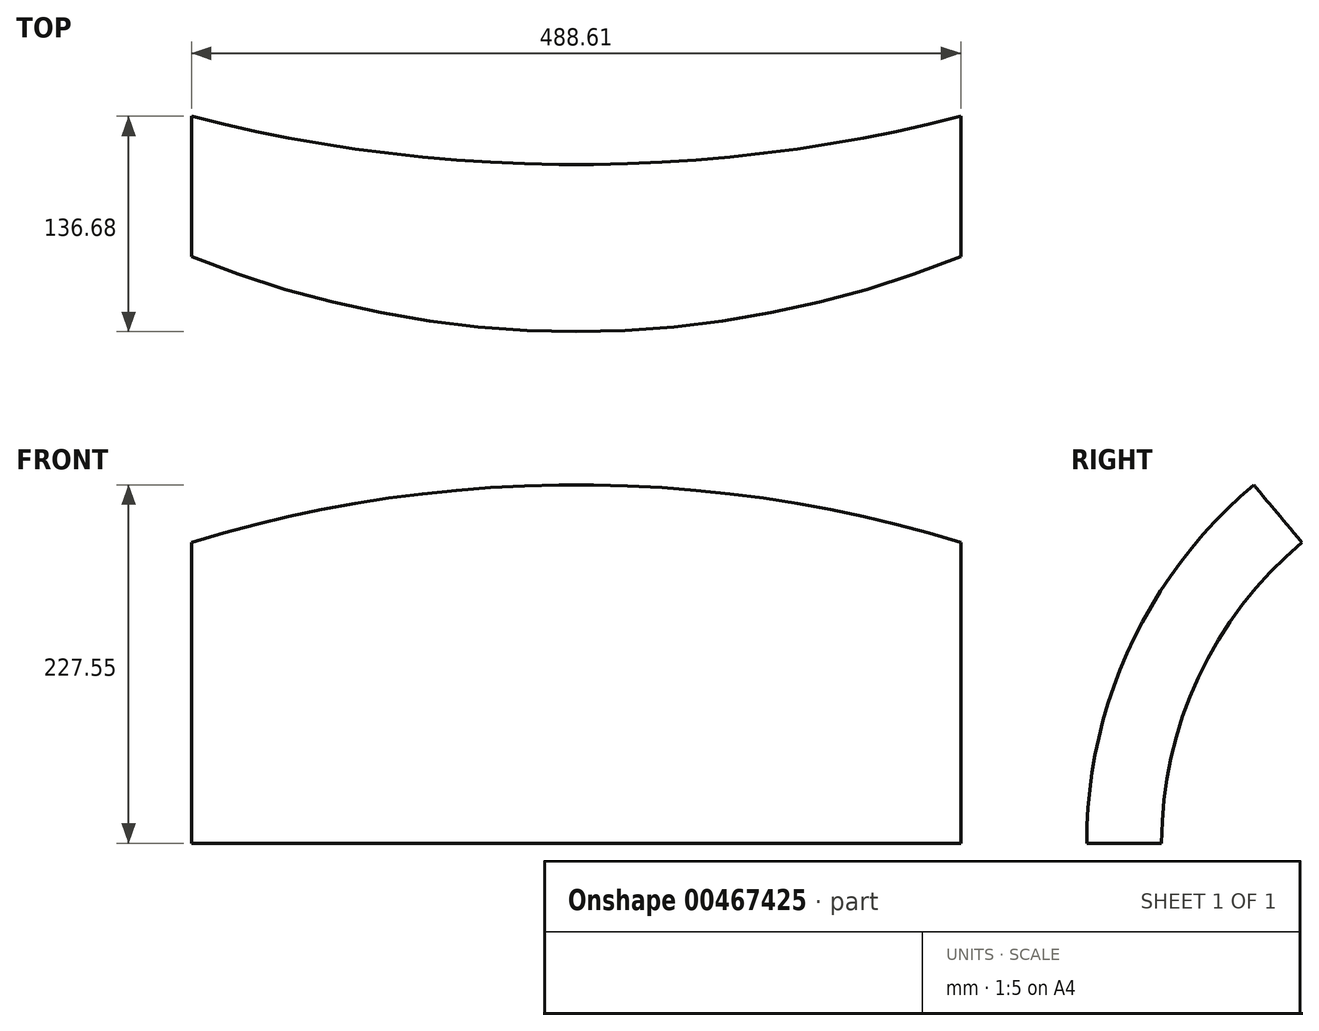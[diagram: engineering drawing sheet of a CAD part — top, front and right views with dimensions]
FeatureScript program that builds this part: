
annotation { "Feature Type Name" : "Feature", "Feature Type Description" : "" }
export const myFeature = defineFeature(function(context is Context, id is Id, definition is map)
    precondition{}
    {
        {
            var Q0;
            Q0=qCreatedBy(makeId("Front.planeOp"),FACE);
            var sketch = newSketch(context, id + "F0", { "sketchPlane" : qUnion([Q0])});
            skArc(sketch, "E0", {"start": v(245.95, 29.96) * mm, "mid": v(1.65, 77.53) * mm, "end": v(-242.66, 29.96) * mm});
            skPoint(sketch, "E0.first.point", {"position": v(-527.6, -194.3) * mm});
            skPoint(sketch, "E0.second.point", {"position": v(0, 77.53) * mm});
            skPoint(sketch, "E0.third.point", {"position": v(523.07, -183.61) * mm});
            skLineSegment(sketch, "E1", {"start": v(-490.34, -219.5) * mm, "end": v(514.5, -219.5) * mm});
            skSolve(sketch);
        }
        {
            var Q0;
            Q0 = qSketchRegion(id + "F0", true);
            var Q1;
            Q1=sQuery(id+"F0.wireOp",EDGE,"E0");
            var Q2;
            Q2=sQuery(id+"F0.wireOp",EDGE,"E1");
            revolve(context, id + "F1", {"bodyType" : ToolBodyType.SURFACE, "entities" : qUnion([Q0]), "surfaceEntities" : qUnion([Q1]), "axis" : qUnion([Q2]), "revolveType" : RevolveType.TWO_DIRECTIONS, "angle" : 90 * degree, "angleBack" : 40 * degree});
        }
    });
